# Revit family: Doors_Sliding_Hajom_Architect_Type-SD-GH
name_source: partatom
category: Doors
revit_build: Autodesk Revit 2018 (Build: 20170223_1515(x64)
units: mm (PartAtom-declared; Revit-internal decimal feet)

## family parameters
Always vertical = Yes
Cut with Voids When Loaded = No
Host = Wall
OmniClass Number = 23.30.10.00
OmniClass Title = Doors
Room Calculation Point = No
Shared = No

## types (1)
- Architect - Type SD GH
    AssetType = Fixed
    BIMObjectName = Doors_Sliding_Hajom_Architect_Type-SD-GH
    Brand = Hajom
    Category = Doors
    Default Sill Height = 0 mm  [stored 0 ft]
    DurationUnit = Year
    Height = 0 mm  [stored 0 ft]
    Manufacturer = Hajom
    ManufacturerName = Hajom
    ManufacturerURL = https://www.hajom.com
    Material = PVC
    Model = Architect - Type SD GH
    NBSDescription = PVC-U doorsets
    NBSReference = 45-25-28/346
    Name = Architect_Type-SD-GH
    NominalDepth = 205 mm  [stored 0.672572 ft]
    Rough Height = 0 mm  [stored 0 ft]
    Rough Width = 0 mm  [stored 0 ft]
    Shape = Rectangular
    Size = 1780-2820x2980-7145x205 mm
    URL = https://www.hajom.com
    Uniclass2 = Pr_30_59
    Uniclass2015Description = Unplasticized polyvinylchloride (PVC-U) doorsets
    Uniclass2015Reference = Pr_30_59_24_92
    Version = 1
    VersionDate = 27/05/2022
    Wall Closure = By host
    WarrantyDurationUnit = Year
    Width = 0 mm  [stored 0 ft]

note: [stored X ft] marks values corroborated as IEEE doubles in the binary element streams (Revit-internal decimal feet)

## geometry (parser evidence)
native form markers: Sweep x31
no freeform markers — native parametric forms only
